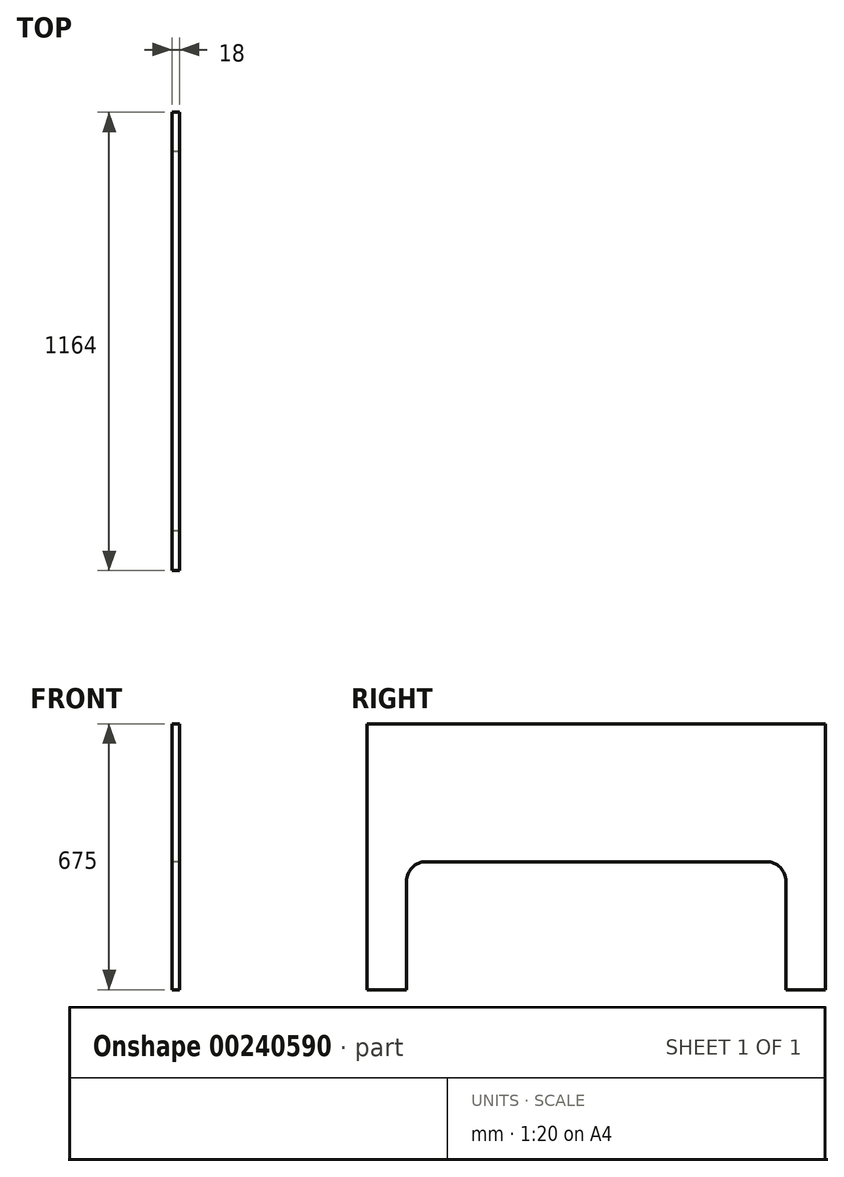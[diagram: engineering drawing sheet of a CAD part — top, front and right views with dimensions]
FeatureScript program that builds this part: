
annotation { "Feature Type Name" : "Feature", "Feature Type Description" : "" }
export const myFeature = defineFeature(function(context is Context, id is Id, definition is map)
    precondition{}
    {
        {
            var Q0;
            Q0=qCreatedBy(makeId("Right.planeOp"),FACE);
            var sketch = newSketch(context, id + "F0", { "sketchPlane" : qUnion([Q0])});
            skLineSegment(sketch, "E0.bottom", {"start": v(0, 0) * mm, "end": v(1164, 0) * mm});
            skLineSegment(sketch, "E0.top", {"start": v(0, 675) * mm, "end": v(1164, 675) * mm});
            skLineSegment(sketch, "E0.left", {"start": v(0, 0) * mm, "end": v(0, 675) * mm});
            skLineSegment(sketch, "E0.right", {"start": v(1164, 0) * mm, "end": v(1164, 675) * mm});
            skLineSegment(sketch, "E1.bottom", {"start": v(100, 0) * mm, "end": v(1064, 0) * mm});
            skLineSegment(sketch, "E1.top", {"start": v(150, 325) * mm, "end": v(1014, 325) * mm});
            skLineSegment(sketch, "E1.left", {"start": v(100, 0) * mm, "end": v(100, 275) * mm});
            skLineSegment(sketch, "E1.right", {"start": v(1064, 0) * mm, "end": v(1064, 275) * mm});
            skPoint(sketch, "E2.visualSharp", {"position": v(100, 325) * mm});
            skArc(sketch, "E2.filletArc", {"start": v(150, 325) * mm, "mid": v(114.64, 310.36) * mm, "end": v(100, 275) * mm});
            skPoint(sketch, "E3.visualSharp", {"position": v(1064, 325) * mm});
            skArc(sketch, "E3.filletArc", {"start": v(1064, 275) * mm, "mid": v(1049.36, 310.36) * mm, "end": v(1014, 325) * mm});
            skSolve(sketch);
        }
        {
            var Q0;
            Q0=makeQuery(id+"F0.imprint","IMPRINT",FACE,{"disambiguationData":[TD([[makeQuery(id+"F0.imprint","IMPRINT",EDGE,{"derivedFrom":sQuery(id+"F0.wireOp",EDGE,"E0.top")}),-1.0]])]});
            extrude(context, id + "F1", {"entities" : qUnion([Q0]), "depth" : 18 * mm});
        }
    });
